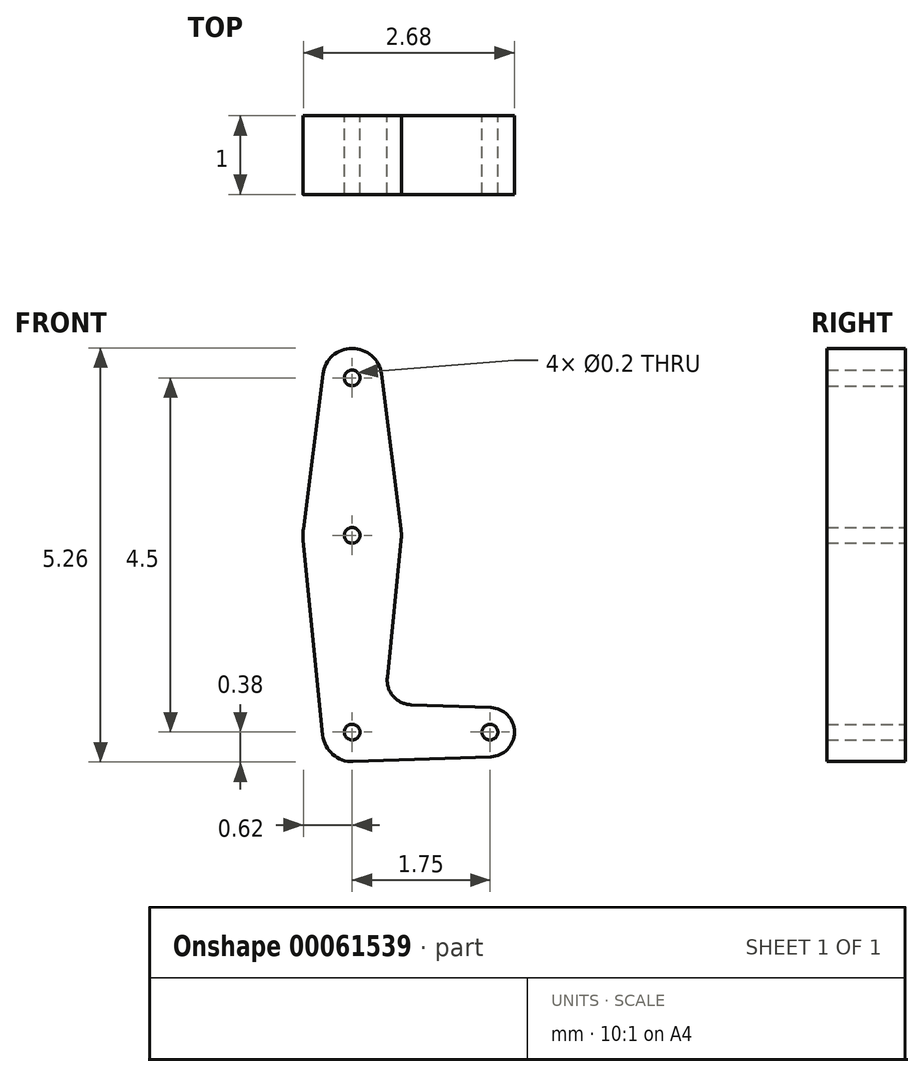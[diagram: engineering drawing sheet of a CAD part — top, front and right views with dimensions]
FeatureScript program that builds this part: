
annotation { "Feature Type Name" : "Feature", "Feature Type Description" : "" }
export const myFeature = defineFeature(function(context is Context, id is Id, definition is map)
    precondition{}
    {
        {
            var Q0;
            Q0=qCreatedBy(makeId("Front.planeOp"),FACE);
            var sketch = newSketch(context, id + "F0", { "sketchPlane" : qUnion([Q0])});
            skCircle(sketch, "E0", {"center": v(0, 0) * mm, "radius": 0.38 * mm});
            skLineSegment(sketch, "E1", {"start": v(0, 0) * mm, "end": v(0, 2.5) * mm});
            skCircle(sketch, "E2", {"center": v(0, 2.5) * mm, "radius": 0.62 * mm});
            skLineSegment(sketch, "E3", {"start": v(0, 2.5) * mm, "end": v(0, 4.5) * mm});
            skCircle(sketch, "E4", {"center": v(0, 4.5) * mm, "radius": 0.38 * mm});
            skLineSegment(sketch, "E5", {"start": v(0, 0) * mm, "end": v(1.75, 0) * mm});
            skCircle(sketch, "E6", {"center": v(1.75, 0) * mm, "radius": 0.31 * mm});
            skLineSegment(sketch, "E7", {"start": v(-0.37, 4.55) * mm, "end": v(-0.62, 2.58) * mm});
            skLineSegment(sketch, "E8", {"start": v(-0.62, 2.44) * mm, "end": v(-0.37, -0.04) * mm});
            skLineSegment(sketch, "E9", {"start": v(0.37, 4.55) * mm, "end": v(0.62, 2.58) * mm});
            skLineSegment(sketch, "E10", {"start": v(0.62, 2.44) * mm, "end": v(0.45, 0.7) * mm});
            skLineSegment(sketch, "E11", {"start": v(0.75, 0.35) * mm, "end": v(1.76, 0.31) * mm});
            skLineSegment(sketch, "E12", {"start": v(0.01, -0.37) * mm, "end": v(1.76, -0.31) * mm});
            skCircle(sketch, "E13", {"center": v(0, 4.5) * mm, "radius": 0.1 * mm});
            skCircle(sketch, "E14", {"center": v(0, 2.5) * mm, "radius": 0.1 * mm});
            skCircle(sketch, "E15", {"center": v(0, 0) * mm, "radius": 0.1 * mm});
            skCircle(sketch, "E16", {"center": v(1.75, 0) * mm, "radius": 0.1 * mm});
            skArc(sketch, "E17.filletArc", {"start": v(0.45, 0.7) * mm, "mid": v(0.52, 0.46) * mm, "end": v(0.75, 0.35) * mm});
            skSolve(sketch);
        }
        {
            var Q0;
            {var subQ0=sQuery(id+"F0.wireOp",EDGE,"E10");Q0=makeQuery(id+"F0.imprint","IMPRINT",FACE,{"disambiguationData":[TD([[makeQuery(id+"F0.imprint","IMPRINT",EDGE,{"derivedFrom":subQ0}),-1.0]])]});}
            var Q1;
            {var subQ0=sQuery(id+"F0.wireOp",EDGE,"E12");Q1=makeQuery(id+"F0.imprint","IMPRINT",FACE,{"disambiguationData":[TD([[makeQuery(id+"F0.imprint","IMPRINT",EDGE,{"derivedFrom":subQ0}),1.0]])]});}
            var Q2;
            Q2=makeQuery(id+"F0.imprint","IMPRINT",FACE,{"disambiguationData":[TD([[makeQuery(id+"F0.imprint","IMPRINT",EDGE,{"derivedFrom":sQuery(id+"F0.wireOp",EDGE,"E16")}),-1.0]])]});
            var Q3;
            {var subQ0=sQuery(id+"F0.wireOp",EDGE,"E8");Q3=makeQuery(id+"F0.imprint","IMPRINT",FACE,{"disambiguationData":[TD([[makeQuery(id+"F0.imprint","IMPRINT",EDGE,{"derivedFrom":subQ0}),1.0]])]});}
            var Q4;
            {var subQ1=sQuery(id+"F0.wireOp",EDGE,"E0");var subQ8=makeQuery(id+"F0.imprint","INTERSECT",VERTEX,{"derivedFrom":[subQ1,sQuery(id+"F0.wireOp",EDGE,"E8")]});Q4=makeQuery(id+"F0.imprint","IMPRINT",FACE,{"disambiguationData":[TD([[makeQuery(id+"F0.imprint","IMPRINT",EDGE,{"disambiguationData":[TD([[subQ8,1.0]])],"derivedFrom":subQ1}),1.0]])]});}
            var Q5;
            {var subQ0=sQuery(id+"F0.wireOp",EDGE,"E1");var subQ1=sQuery(id+"F0.wireOp",EDGE,"E0");var subQ2=makeQuery(id+"F0.imprint","INTERSECT",VERTEX,{"derivedFrom":[subQ1,subQ0]});Q5=makeQuery(id+"F0.imprint","IMPRINT",FACE,{"disambiguationData":[TD([[makeQuery(id+"F0.imprint","IMPRINT",EDGE,{"disambiguationData":[TD([[subQ2,1.0]])],"derivedFrom":subQ1}),1.0]])]});}
            var Q6;
            {var subQ0=sQuery(id+"F0.wireOp",EDGE,"E7");Q6=makeQuery(id+"F0.imprint","IMPRINT",FACE,{"disambiguationData":[TD([[makeQuery(id+"F0.imprint","IMPRINT",EDGE,{"derivedFrom":subQ0}),1.0]])]});}
            var Q7;
            {var subQ0=sQuery(id+"F0.wireOp",EDGE,"E2");var subQ2=sQuery(id+"F0.wireOp",EDGE,"E1");var subQ3=makeQuery(id+"F0.imprint","INTERSECT",VERTEX,{"derivedFrom":[subQ2,subQ0]});Q7=makeQuery(id+"F0.imprint","IMPRINT",FACE,{"disambiguationData":[TD([[makeQuery(id+"F0.imprint","IMPRINT",EDGE,{"disambiguationData":[TD([[subQ3,-1.0]])],"derivedFrom":subQ2}),1.0]])]});}
            var Q8;
            {var subQ0=sQuery(id+"F0.wireOp",EDGE,"E2");var subQ3=sQuery(id+"F0.wireOp",EDGE,"E1");var subQ4=makeQuery(id+"F0.imprint","INTERSECT",VERTEX,{"derivedFrom":[subQ3,subQ0]});Q8=makeQuery(id+"F0.imprint","IMPRINT",FACE,{"disambiguationData":[TD([[makeQuery(id+"F0.imprint","IMPRINT",EDGE,{"disambiguationData":[TD([[subQ4,-1.0]])],"derivedFrom":subQ3}),-1.0]])]});}
            var Q9;
            {var subQ0=sQuery(id+"F0.wireOp",EDGE,"E9");Q9=makeQuery(id+"F0.imprint","IMPRINT",FACE,{"disambiguationData":[TD([[makeQuery(id+"F0.imprint","IMPRINT",EDGE,{"derivedFrom":subQ0}),-1.0]])]});}
            var Q10;
            Q10=makeQuery(id+"F0.imprint","IMPRINT",FACE,{"disambiguationData":[TD([[makeQuery(id+"F0.imprint","IMPRINT",EDGE,{"derivedFrom":sQuery(id+"F0.wireOp",EDGE,"E13")}),-1.0]])]});
            extrude(context, id + "F1", {"entities" : qUnion([Q0, Q1, Q2, Q3, Q4, Q5, Q6, Q7, Q8, Q9, Q10]), "depth" : 1 * mm});
        }
    });
